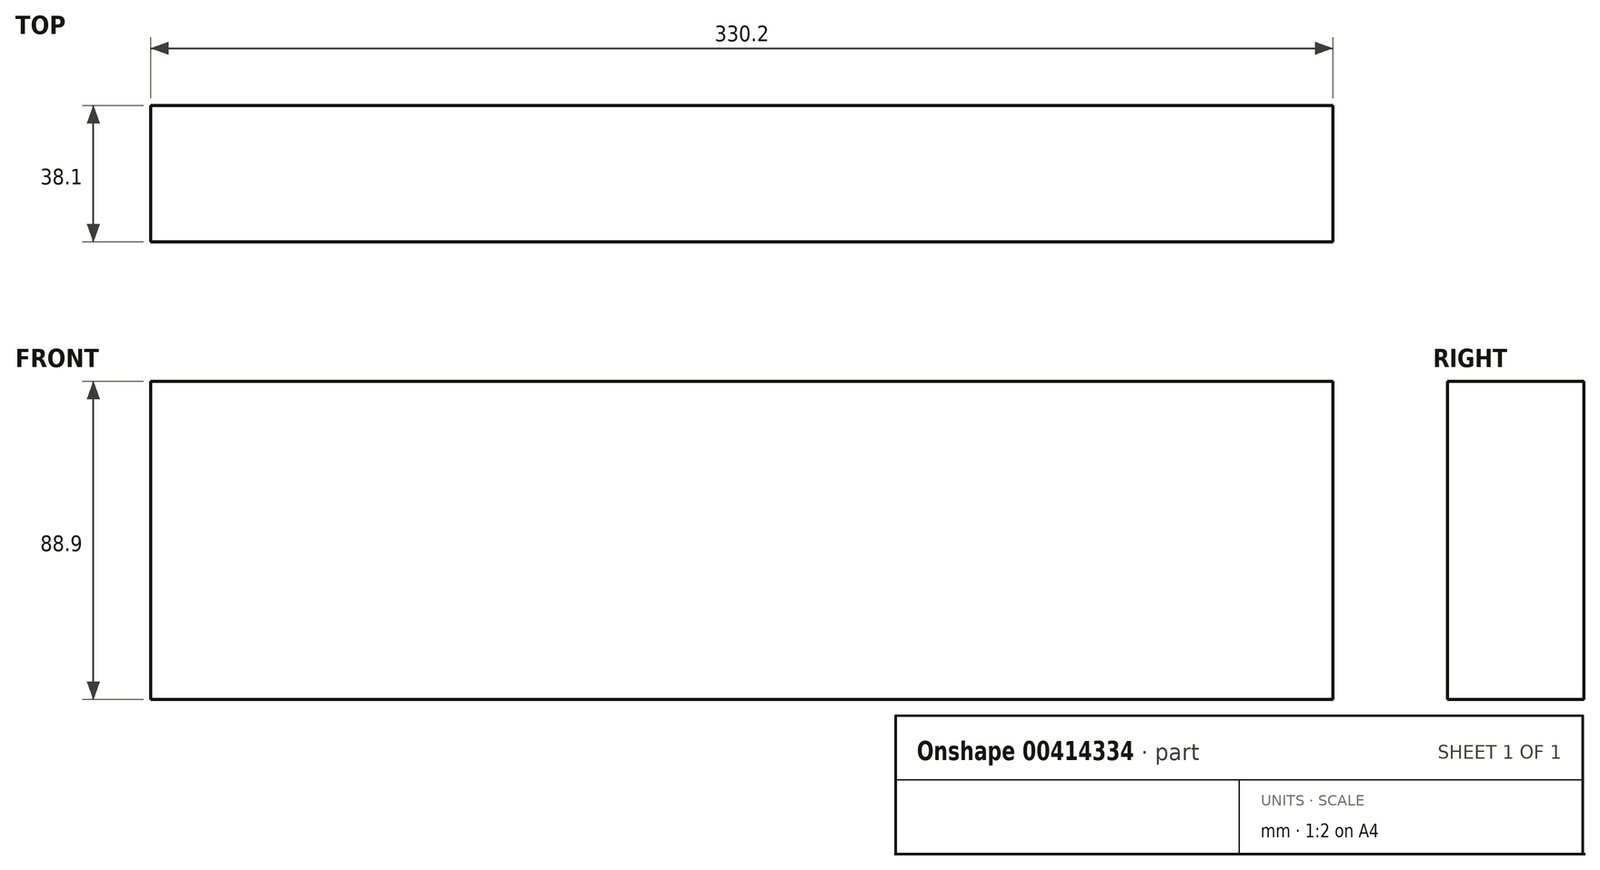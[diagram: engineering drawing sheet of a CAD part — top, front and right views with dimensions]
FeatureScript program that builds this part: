
annotation { "Feature Type Name" : "Feature", "Feature Type Description" : "" }
export const myFeature = defineFeature(function(context is Context, id is Id, definition is map)
    precondition{}
    {
        {
            var Q0;
            Q0=qCreatedBy(makeId("Top.planeOp"),FACE);
            var sketch = newSketch(context, id + "F0", { "sketchPlane" : qUnion([Q0])});
            skLineSegment(sketch, "E0.bottom", {"start": v(165.1, 19.05) * mm, "end": v(-165.1, 19.05) * mm});
            skLineSegment(sketch, "E0.top", {"start": v(165.1, -19.05) * mm, "end": v(-165.1, -19.05) * mm});
            skLineSegment(sketch, "E0.left", {"start": v(165.1, 19.05) * mm, "end": v(165.1, -19.05) * mm});
            skLineSegment(sketch, "E0.right", {"start": v(-165.1, 19.05) * mm, "end": v(-165.1, -19.05) * mm});
            skPoint(sketch, "E0.middle", {"position": v(0, 0) * mm});
            skSolve(sketch);
        }
        {
            var Q0;
            Q0=makeQuery(id+"F0.imprint","IMPRINT",FACE,{"disambiguationData":[TD([[makeQuery(id+"F0.imprint","IMPRINT",EDGE,{"derivedFrom":sQuery(id+"F0.wireOp",EDGE,"E0.bottom")}),1.0]])]});
            extrude(context, id + "F1", {"entities" : qUnion([Q0]), "depth" : 88.9 * mm});
        }
    });
